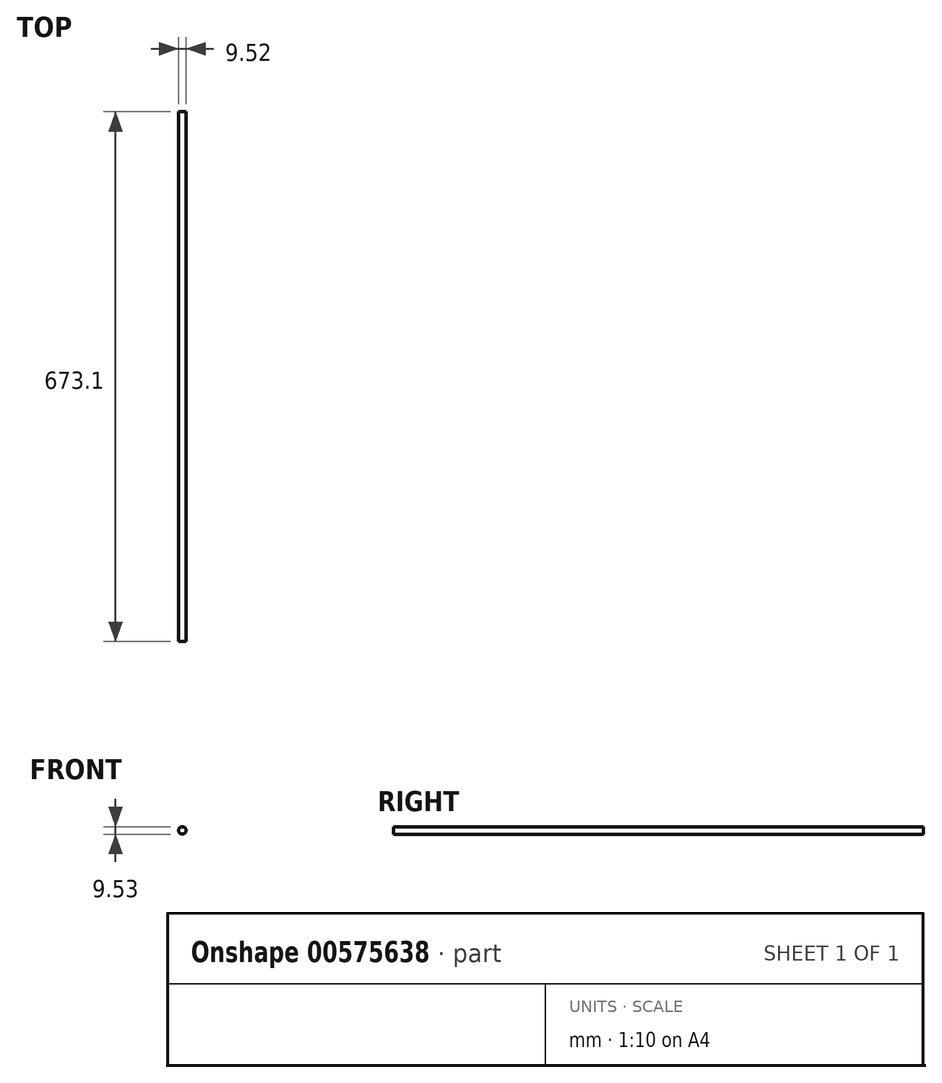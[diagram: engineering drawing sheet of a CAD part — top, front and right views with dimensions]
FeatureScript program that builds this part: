
annotation { "Feature Type Name" : "Feature", "Feature Type Description" : "" }
export const myFeature = defineFeature(function(context is Context, id is Id, definition is map)
    precondition{}
    {
        {
            var Q0;
            Q0=qCreatedBy(makeId("Front.planeOp"),FACE);
            var sketch = newSketch(context, id + "F0", { "sketchPlane" : qUnion([Q0])});
            skCircle(sketch, "E0", {"center": v(-9.8, 13.16) * mm, "radius": 4.76 * mm});
            skSolve(sketch);
        }
        {
            var Q0;
            Q0=qSketchRegion(id+"F0",true);
            extrude(context, id + "F1", {"entities" : qUnion([Q0]), "depth" : 673.1 * mm, "offsetDistance" : 25.4 * mm});
        }
    });
